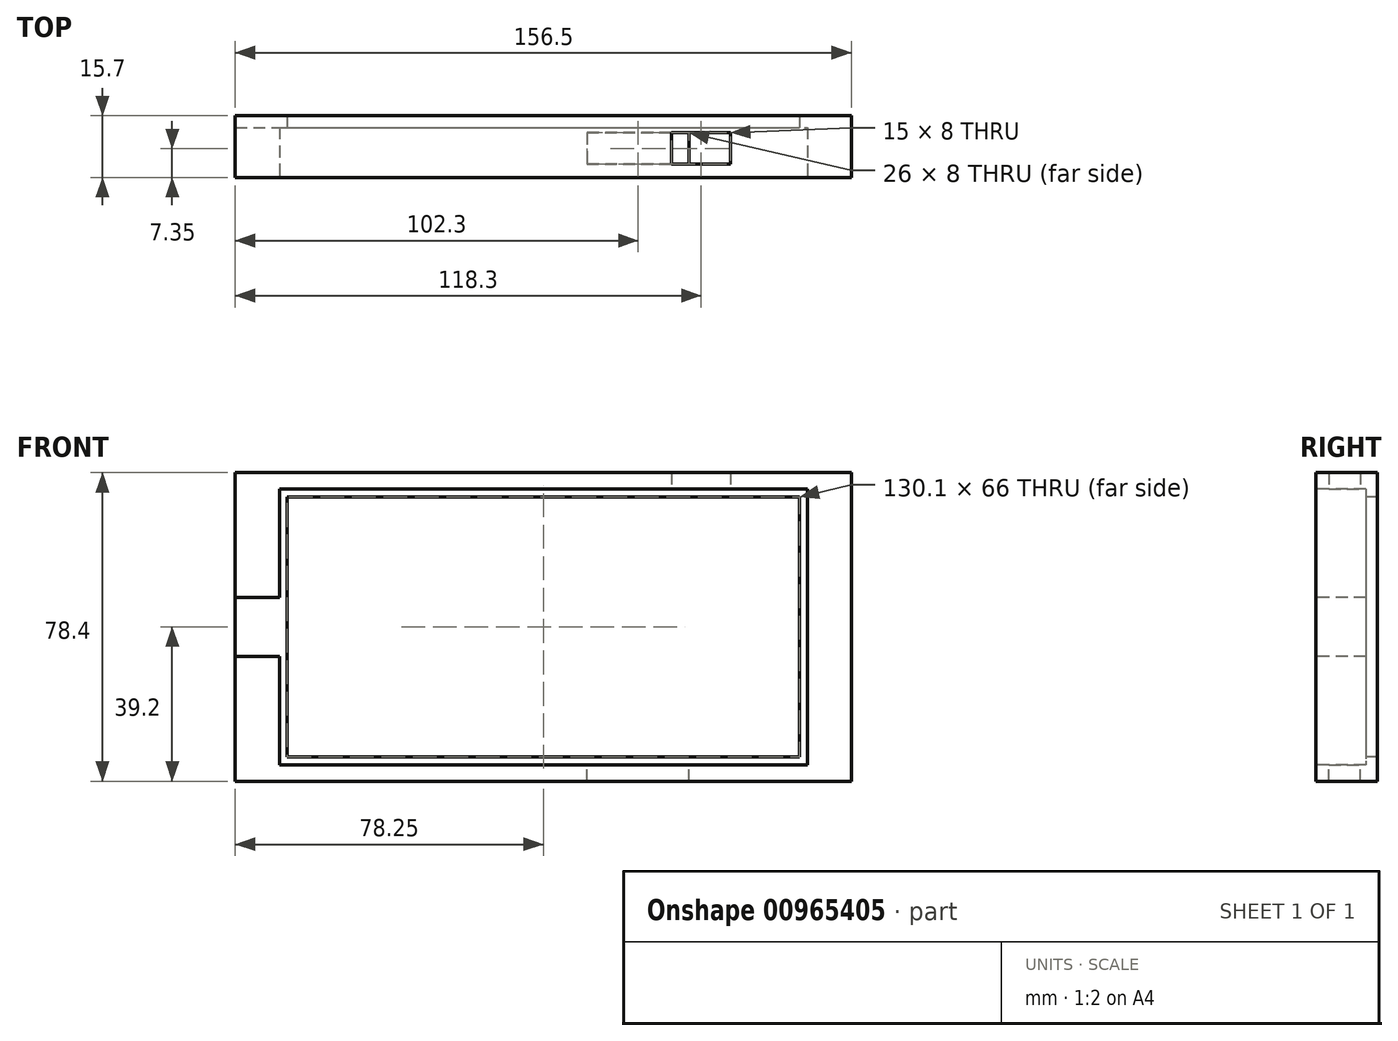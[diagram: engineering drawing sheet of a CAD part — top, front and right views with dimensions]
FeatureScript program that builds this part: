
annotation { "Feature Type Name" : "Feature", "Feature Type Description" : "" }
export const myFeature = defineFeature(function(context is Context, id is Id, definition is map)
    precondition{}
    {
        {
            var Q0;
            Q0=qCreatedBy(makeId("Front.planeOp"),FACE);
            var sketch = newSketch(context, id + "F0", { "sketchPlane" : qUnion([Q0])});
            skLineSegment(sketch, "E0.bottom", {"start": v(-67.05, 35) * mm, "end": v(67.05, 35) * mm});
            skLineSegment(sketch, "E0.top", {"start": v(-67.05, -35) * mm, "end": v(67.05, -35) * mm});
            skLineSegment(sketch, "E0.left", {"start": v(-67.05, 35) * mm, "end": v(-67.05, -35) * mm});
            skLineSegment(sketch, "E0.right", {"start": v(67.05, 35) * mm, "end": v(67.05, -35) * mm});
            skPoint(sketch, "E0.middle", {"position": v(0, 0) * mm});
            skLineSegment(sketch, "E1.0", {"start": v(-71.25, 39.2) * mm, "end": v(71.25, 39.2) * mm});
            skLineSegment(sketch, "E1.1", {"start": v(-71.25, 39.2) * mm, "end": v(-71.25, -39.2) * mm});
            skLineSegment(sketch, "E1.2", {"start": v(-71.25, -39.2) * mm, "end": v(71.25, -39.2) * mm});
            skLineSegment(sketch, "E1.3", {"start": v(71.25, 39.2) * mm, "end": v(71.25, -39.2) * mm});
            skLineSegment(sketch, "E2.bottom", {"start": v(-67.05, 35) * mm, "end": v(-65.05, 35) * mm});
            skLineSegment(sketch, "E2.top", {"start": v(-67.05, -35) * mm, "end": v(-65.05, -35) * mm});
            skLineSegment(sketch, "E2.right", {"start": v(-65.05, 35) * mm, "end": v(-65.05, -35) * mm});
            skLineSegment(sketch, "E3.bottom", {"start": v(67.05, 35) * mm, "end": v(65.05, 35) * mm});
            skLineSegment(sketch, "E3.top", {"start": v(67.05, -35) * mm, "end": v(65.05, -35) * mm});
            skLineSegment(sketch, "E3.right", {"start": v(65.05, 35) * mm, "end": v(65.05, -35) * mm});
            skLineSegment(sketch, "E4.bottom", {"start": v(-65.05, 35) * mm, "end": v(65.05, 35) * mm});
            skLineSegment(sketch, "E4.top", {"start": v(-65.05, 33) * mm, "end": v(65.05, 33) * mm});
            skLineSegment(sketch, "E4.left", {"start": v(-65.05, 35) * mm, "end": v(-65.05, 33) * mm});
            skLineSegment(sketch, "E4.right", {"start": v(65.05, 35) * mm, "end": v(65.05, 33) * mm});
            skLineSegment(sketch, "E5.bottom", {"start": v(-65.05, -35) * mm, "end": v(65.05, -35) * mm});
            skLineSegment(sketch, "E5.top", {"start": v(-65.05, -33) * mm, "end": v(65.05, -33) * mm});
            skLineSegment(sketch, "E5.left", {"start": v(-65.05, -35) * mm, "end": v(-65.05, -33) * mm});
            skLineSegment(sketch, "E5.right", {"start": v(65.05, -35) * mm, "end": v(65.05, -33) * mm});
            skLineSegment(sketch, "E6.bottom", {"start": v(-71.25, 39.2) * mm, "end": v(-78.25, 39.2) * mm});
            skLineSegment(sketch, "E6.top", {"start": v(-71.25, -39.2) * mm, "end": v(-78.25, -39.2) * mm});
            skLineSegment(sketch, "E6.right", {"start": v(-78.25, 39.2) * mm, "end": v(-78.25, -39.2) * mm});
            skLineSegment(sketch, "E7.bottom", {"start": v(71.25, 39.2) * mm, "end": v(78.25, 39.2) * mm});
            skLineSegment(sketch, "E7.top", {"start": v(71.25, -39.2) * mm, "end": v(78.25, -39.2) * mm});
            skLineSegment(sketch, "E7.right", {"start": v(78.25, 39.2) * mm, "end": v(78.25, -39.2) * mm});
            skSolve(sketch);
        }
        {
            var Q0;
            {var subQ3=sQuery(id+"F0.wireOp",EDGE,"E0.right");Q0=makeQuery(id+"F0.imprint","IMPRINT",FACE,{"disambiguationData":[TD([[makeQuery(id+"F0.imprint","IMPRINT",EDGE,{"derivedFrom":subQ3}),-1.0]])]});}
            var Q1;
            {var subQ5=sQuery(id+"F0.wireOp",EDGE,"E4.top");Q1=makeQuery(id+"F0.imprint","IMPRINT",FACE,{"disambiguationData":[TD([[makeQuery(id+"F0.imprint","IMPRINT",EDGE,{"derivedFrom":subQ5}),1.0]])]});}
            var Q2;
            {var subQ5=sQuery(id+"F0.wireOp",EDGE,"E0.left");Q2=makeQuery(id+"F0.imprint","IMPRINT",FACE,{"disambiguationData":[TD([[makeQuery(id+"F0.imprint","IMPRINT",EDGE,{"derivedFrom":subQ5}),1.0]])]});}
            var Q3;
            {var subQ5=sQuery(id+"F0.wireOp",EDGE,"E5.top");Q3=makeQuery(id+"F0.imprint","IMPRINT",FACE,{"disambiguationData":[TD([[makeQuery(id+"F0.imprint","IMPRINT",EDGE,{"derivedFrom":subQ5}),-1.0]])]});}
            extrude(context, id + "F1", {"entities" : qUnion([Q0, Q1, Q2, Q3]), "oppositeDirection" : true, "depth" : 3 * mm, "offsetDistance" : 25 * mm});
        }
        {
            var Q0;
            {var subQ1=sQuery(id+"F0.wireOp",EDGE,"E0.left");Q0=makeQuery(id+"F0.imprint","IMPRINT",FACE,{"disambiguationData":[TD([[makeQuery(id+"F0.imprint","IMPRINT",EDGE,{"derivedFrom":subQ1}),-1.0]])]});}
            var Q1;
            Q1=makeQuery(id+"F0.imprint","IMPRINT",FACE,{"disambiguationData":[TD([[makeQuery(id+"F0.imprint","IMPRINT",EDGE,{"derivedFrom":sQuery(id+"F0.wireOp",EDGE,"E1.1")}),-1.0]])]});
            var Q2;
            Q2=makeQuery(id+"F0.imprint","IMPRINT",FACE,{"disambiguationData":[TD([[makeQuery(id+"F0.imprint","IMPRINT",EDGE,{"derivedFrom":sQuery(id+"F0.wireOp",EDGE,"E1.3")}),1.0]])]});
            extrude(context, id + "F2", {"entities" : qUnion([Q0, Q1, Q2]), "operationType" : NewBodyOperationType.ADD, "oppositeDirection" : true, "depth" : 3 * mm, "offsetDistance" : 25 * mm, "hasSecondDirection" : true, "secondDirectionOppositeDirection" : false, "secondDirectionDepth" : 12.7 * mm});
        }
        {
            var Q0;
            Q0=makeQuery(id+"F2.opExtrude","CAP_FACE",FACE,{"disambiguationData":[OSD([sQuery(id+"F0.wireOp",EDGE,"E0.bottom"),sQuery(id+"F0.wireOp",EDGE,"E0.top"),sQuery(id+"F0.wireOp",EDGE,"E0.left"),sQuery(id+"F0.wireOp",EDGE,"E0.right"),sQuery(id+"F0.wireOp",EDGE,"E1.0"),sQuery(id+"F0.wireOp",EDGE,"E1.2"),sQuery(id+"F0.wireOp",EDGE,"E6.bottom"),sQuery(id+"F0.wireOp",EDGE,"E6.top"),sQuery(id+"F0.wireOp",EDGE,"E6.right"),sQuery(id+"F0.wireOp",EDGE,"E7.bottom"),sQuery(id+"F0.wireOp",EDGE,"E7.top"),sQuery(id+"F0.wireOp",EDGE,"E7.right")])],"isStart":true});
            var sketch = newSketch(context, id + "F3", { "sketchPlane" : qUnion([Q0])});
            skLineSegment(sketch, "E8", {"start": v(-67.05, 0) * mm, "end": v(-78.25, 0) * mm});
            skLineSegment(sketch, "E9", {"start": v(-72.65, 0) * mm, "end": v(-72.65, 39.2) * mm});
            skLineSegment(sketch, "E10", {"start": v(-72.65, 0) * mm, "end": v(-72.65, -39.2) * mm});
            skLineSegment(sketch, "E11.bottom", {"start": v(-78.25, 7.5) * mm, "end": v(-67.05, 7.5) * mm});
            skLineSegment(sketch, "E11.top", {"start": v(-78.25, -7.5) * mm, "end": v(-67.05, -7.5) * mm});
            skLineSegment(sketch, "E11.left", {"start": v(-78.25, 7.5) * mm, "end": v(-78.25, -7.5) * mm});
            skLineSegment(sketch, "E11.right", {"start": v(-67.05, 7.5) * mm, "end": v(-67.05, -7.5) * mm});
            skPoint(sketch, "E11.middle", {"position": v(-72.65, 0) * mm});
            skSolve(sketch);
        }
        {
            var Q0;
            {var subQ0=sQuery(id+"F3.wireOp",EDGE,"E11.left");var subQ1=sQuery(id+"F3.wireOp",EDGE,"E8");var subQ2=makeQuery(id+"F3.imprint","INTERSECT",VERTEX,{"derivedFrom":[subQ1,subQ0]});Q0=makeQuery(id+"F3.imprint","IMPRINT",FACE,{"disambiguationData":[TD([[makeQuery(id+"F3.imprint","IMPRINT",EDGE,{"disambiguationData":[TD([[subQ2,1.0]])],"derivedFrom":subQ1}),-1.0]])]});}
            var Q1;
            {var subQ0=sQuery(id+"F3.wireOp",EDGE,"E11.right");var subQ1=sQuery(id+"F3.wireOp",EDGE,"E8");var subQ2=makeQuery(id+"F3.imprint","INTERSECT",VERTEX,{"derivedFrom":[subQ1,subQ0]});Q1=makeQuery(id+"F3.imprint","IMPRINT",FACE,{"disambiguationData":[TD([[makeQuery(id+"F3.imprint","IMPRINT",EDGE,{"disambiguationData":[TD([[subQ2,-1.0]])],"derivedFrom":subQ1}),-1.0]])]});}
            var Q2;
            {var subQ0=sQuery(id+"F3.wireOp",EDGE,"E11.right");var subQ1=sQuery(id+"F3.wireOp",EDGE,"E8");var subQ2=makeQuery(id+"F3.imprint","INTERSECT",VERTEX,{"derivedFrom":[subQ1,subQ0]});Q2=makeQuery(id+"F3.imprint","IMPRINT",FACE,{"disambiguationData":[TD([[makeQuery(id+"F3.imprint","IMPRINT",EDGE,{"disambiguationData":[TD([[subQ2,-1.0]])],"derivedFrom":subQ1}),1.0]])]});}
            var Q3;
            {var subQ0=sQuery(id+"F3.wireOp",EDGE,"E11.left");var subQ1=sQuery(id+"F3.wireOp",EDGE,"E8");var subQ2=makeQuery(id+"F3.imprint","INTERSECT",VERTEX,{"derivedFrom":[subQ1,subQ0]});Q3=makeQuery(id+"F3.imprint","IMPRINT",FACE,{"disambiguationData":[TD([[makeQuery(id+"F3.imprint","IMPRINT",EDGE,{"disambiguationData":[TD([[subQ2,1.0]])],"derivedFrom":subQ1}),1.0]])]});}
            extrude(context, id + "F4", {"entities" : qUnion([Q0, Q1, Q2, Q3]), "operationType" : NewBodyOperationType.REMOVE, "oppositeDirection" : true, "depth" : 12.7 * mm, "offsetDistance" : 25 * mm});
        }
        {
            var Q0;
            Q0=makeQuery(id+"F2.opExtrude","SWEPT_FACE",FACE,{"disambiguationData":[OSD([sQuery(id+"F0.wireOp",EDGE,"E0.bottom")])]});
            var sketch = newSketch(context, id + "F5", { "sketchPlane" : qUnion([Q0])});
            skLineSegment(sketch, "E12", {"start": v(67.05, 6.35) * mm, "end": v(40.05, 6.35) * mm});
            skLineSegment(sketch, "E13.bottom", {"start": v(47.55, 9.35) * mm, "end": v(32.55, 9.35) * mm});
            skLineSegment(sketch, "E13.top", {"start": v(47.55, 3.35) * mm, "end": v(32.55, 3.35) * mm});
            skLineSegment(sketch, "E13.left", {"start": v(47.55, 9.35) * mm, "end": v(47.55, 3.35) * mm});
            skLineSegment(sketch, "E13.right", {"start": v(32.55, 9.35) * mm, "end": v(32.55, 3.35) * mm});
            skPoint(sketch, "E13.middle", {"position": v(40.05, 6.35) * mm});
            skSolve(sketch);
        }
        {
            var Q0;
            {var subQ3=sQuery(id+"F5.wireOp",EDGE,"E13.bottom");Q0=makeQuery(id+"F5.imprint","IMPRINT",FACE,{"disambiguationData":[TD([[makeQuery(id+"F5.imprint","IMPRINT",EDGE,{"derivedFrom":subQ3}),1.0]])]});}
            extrude(context, id + "F6", {"entities" : qUnion([Q0]), "operationType" : NewBodyOperationType.REMOVE, "endBound" : BoundingType.THROUGH_ALL, "oppositeDirection" : true, "depth" : 25 * mm, "offsetDistance" : 25 * mm});
        }
        {
            var Q0;
            Q0=makeQuery(id+"F2.opExtrude","SWEPT_FACE",FACE,{"disambiguationData":[OSD([sQuery(id+"F0.wireOp",EDGE,"E0.top")])]});
            var sketch = newSketch(context, id + "F7", { "sketchPlane" : qUnion([Q0])});
            skLineSegment(sketch, "E14", {"start": v(67.05, -6.35) * mm, "end": v(24.05, -6.35) * mm});
            skLineSegment(sketch, "E15.bottom", {"start": v(37.05, -9.35) * mm, "end": v(11.05, -9.35) * mm});
            skLineSegment(sketch, "E15.top", {"start": v(37.05, -3.35) * mm, "end": v(11.05, -3.35) * mm});
            skLineSegment(sketch, "E15.left", {"start": v(37.05, -9.35) * mm, "end": v(37.05, -3.35) * mm});
            skLineSegment(sketch, "E15.right", {"start": v(11.05, -9.35) * mm, "end": v(11.05, -3.35) * mm});
            skPoint(sketch, "E15.middle", {"position": v(24.05, -6.35) * mm});
            skSolve(sketch);
        }
        {
            var Q0;
            {var subQ3=sQuery(id+"F7.wireOp",EDGE,"E15.bottom");Q0=makeQuery(id+"F7.imprint","IMPRINT",FACE,{"disambiguationData":[TD([[makeQuery(id+"F7.imprint","IMPRINT",EDGE,{"derivedFrom":subQ3}),-1.0]])]});}
            extrude(context, id + "F8", {"entities" : qUnion([Q0]), "operationType" : NewBodyOperationType.REMOVE, "endBound" : BoundingType.THROUGH_ALL, "oppositeDirection" : true, "depth" : 25 * mm, "offsetDistance" : 25 * mm});
        }
        {
            var Q0;
            Q0=makeQuery(id+"F8.boolean.opBoolean","COPY",FACE,{"derivedFrom":makeQuery(id+"F8.opExtrude","SWEPT_FACE",FACE,{"disambiguationData":[OSD([sQuery(id+"F7.wireOp",EDGE,"E15.top")])]})});
            extrude(context, id + "F9", {"entities" : qUnion([Q0]), "operationType" : NewBodyOperationType.REMOVE, "oppositeDirection" : true, "depth" : 2 * mm, "offsetDistance" : 25 * mm});
        }
        {
            var Q0;
            Q0=makeQuery(id+"F6.boolean.opBoolean","COPY",FACE,{"derivedFrom":makeQuery(id+"F6.opExtrude","SWEPT_FACE",FACE,{"disambiguationData":[OSD([sQuery(id+"F5.wireOp",EDGE,"E13.top")])]})});
            extrude(context, id + "F10", {"entities" : qUnion([Q0]), "operationType" : NewBodyOperationType.REMOVE, "oppositeDirection" : true, "depth" : 2 * mm, "offsetDistance" : 25 * mm});
        }
    });
